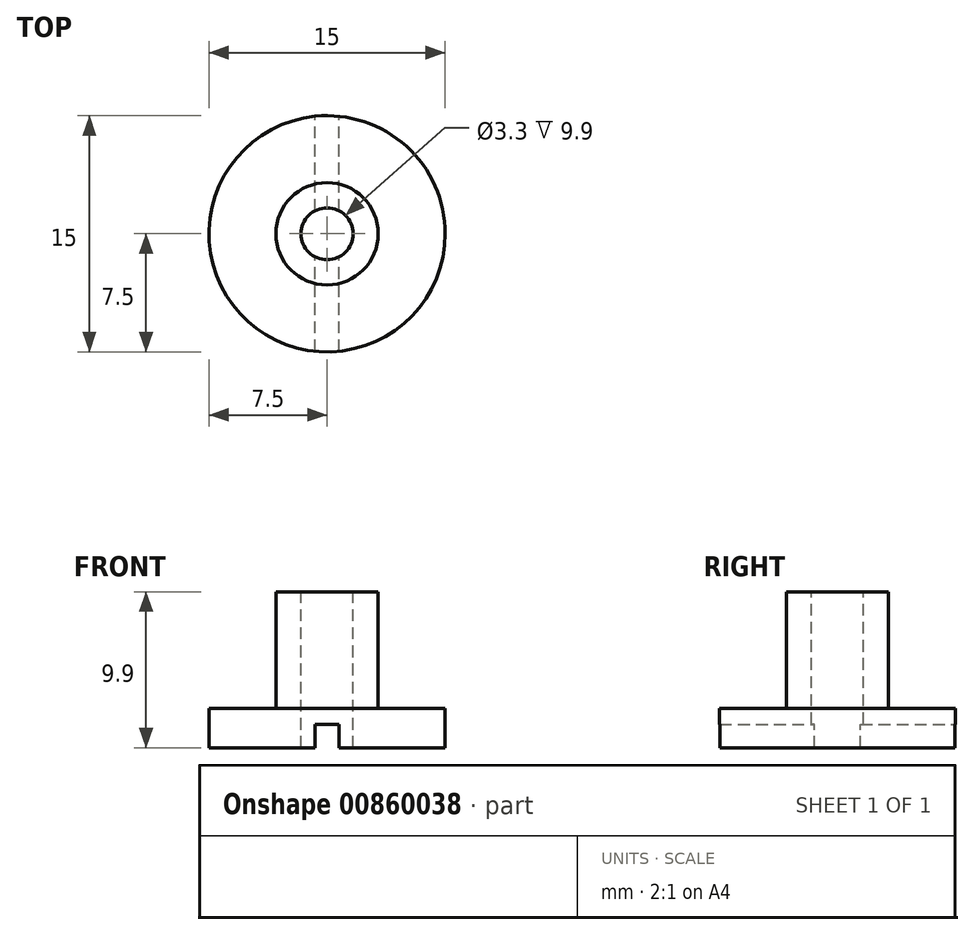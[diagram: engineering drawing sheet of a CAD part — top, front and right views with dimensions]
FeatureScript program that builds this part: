
annotation { "Feature Type Name" : "Feature", "Feature Type Description" : "" }
export const myFeature = defineFeature(function(context is Context, id is Id, definition is map)
    precondition{}
    {
        {
            var Q0;
            Q0=qCreatedBy(makeId("Top.planeOp"),FACE);
            var sketch = newSketch(context, id + "F0", { "sketchPlane" : qUnion([Q0])});
            skCircle(sketch, "E0", {"center": v(0, 0) * mm, "radius": 7.5 * mm});
            skSolve(sketch);
        }
        {
            var Q0;
            Q0=makeQuery(id+"F0.imprint","IMPRINT",FACE,{"disambiguationData":[TD([[makeQuery(id+"F0.imprint","IMPRINT",EDGE,{"derivedFrom":sQuery(id+"F0.wireOp",EDGE,"E0")}),1.0]])]});
            extrude(context, id + "F1", {"entities" : qUnion([Q0]), "depth" : 2.5 * mm, "offsetDistance" : 25 * mm});
        }
        {
            var Q0;
            Q0=makeQuery(id+"F1.opExtrude","CAP_FACE",FACE,{"disambiguationData":[OSD([sQuery(id+"F0.wireOp",EDGE,"E0")])],"isStart":false});
            var sketch = newSketch(context, id + "F2", { "sketchPlane" : qUnion([Q0])});
            skCircle(sketch, "E1", {"center": v(0, 0) * mm, "radius": 3.25 * mm});
            skSolve(sketch);
        }
        {
            var Q0;
            Q0 = qSketchRegion(id + "F2", true);
            extrude(context, id + "F3", {"entities" : qUnion([Q0]), "operationType" : NewBodyOperationType.ADD, "depth" : 7.4 * mm, "offsetDistance" : 25 * mm});
        }
        {
            var Q0;
            Q0=makeQuery(id+"F1.opExtrude","CAP_FACE",FACE,{"disambiguationData":[OSD([sQuery(id+"F0.wireOp",EDGE,"E0")])],"isStart":true});
            var sketch = newSketch(context, id + "F4", { "sketchPlane" : qUnion([Q0])});
            skLineSegment(sketch, "E2.bottom", {"start": v(0.75, 8) * mm, "end": v(-0.75, 8) * mm});
            skLineSegment(sketch, "E2.top", {"start": v(0.75, -8) * mm, "end": v(-0.75, -8) * mm});
            skLineSegment(sketch, "E2.left", {"start": v(0.75, 8) * mm, "end": v(0.75, -8) * mm});
            skLineSegment(sketch, "E2.right", {"start": v(-0.75, 8) * mm, "end": v(-0.75, -8) * mm});
            skPoint(sketch, "E2.middle", {"position": v(0, 0) * mm});
            skSolve(sketch);
        }
        {
            var Q0;
            Q0 = qSketchRegion(id + "F4", true);
            extrude(context, id + "F5", {"entities" : qUnion([Q0]), "operationType" : NewBodyOperationType.REMOVE, "oppositeDirection" : true, "depth" : 1.5 * mm, "offsetDistance" : 25 * mm});
        }
        {
            var Q0;
            Q0=makeQuery(id+"F3.opExtrude","CAP_FACE",FACE,{"disambiguationData":[OSD([sQuery(id+"F2.wireOp",EDGE,"E1")])],"isStart":false});
            var sketch = newSketch(context, id + "F6", { "sketchPlane" : qUnion([Q0])});
            skPoint(sketch, "E3", {"position": v(0, 0) * mm});
            skSolve(sketch);
        }
        {
            var Q0;
            Q0=sQuery(id+"F6.wireOp",VERTEX,"E3");
            var Q1;
            Q1=makeQuery(id+"F1.opExtrude","SWEPT_BODY",BODY,{"disambiguationData":[OSD([sQuery(id+"F0.wireOp",EDGE,"E0")])]});
            hole(context, id + "F7", {"style" : HoleStyle.SIMPLE, "endStyle" : HoleEndStyle.THROUGH, "standardTappedOrClearance" : lookupTablePath({ "standard" : "ISO", "engagement" : "75%", "pitch" : "0.7 mm", "size" : "M4", "type" : "Tapped" }), "standardBlindInLast" : lookupTablePath({ "standard" : "ISO", "engagement" : "75%", "pitch" : "0.7 mm", "size" : "M4", "type" : "Tapped" }), "holeDiameter" : 3.3 * mm, "majorDiameter" : 4 * mm, "showTappedDepth" : true, "isTappedThrough" : true, "tappedDepth" : 3.9 * mm, "tapClearance" : 3, "locations" : qUnion([Q0]), "scope" : qUnion([Q1])});
        }
    });
